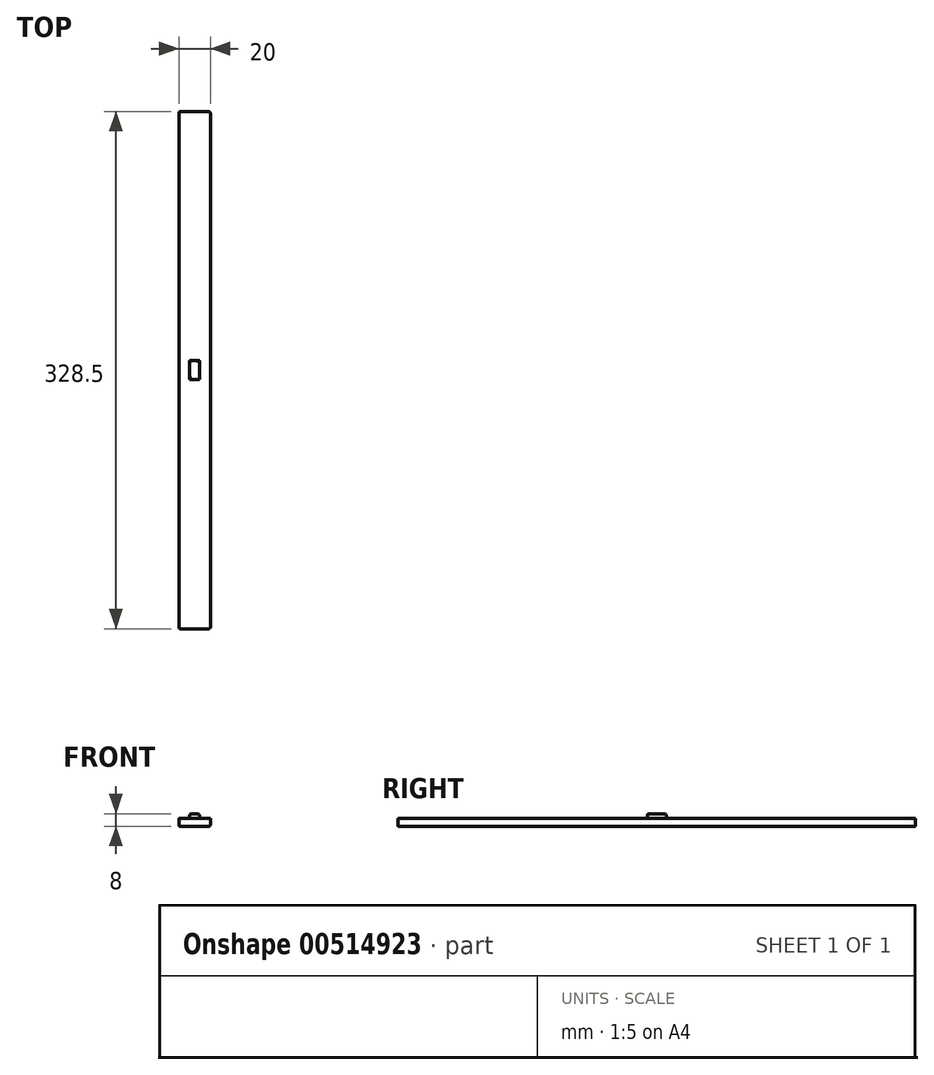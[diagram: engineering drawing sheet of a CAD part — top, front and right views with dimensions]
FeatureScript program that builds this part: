
annotation { "Feature Type Name" : "Feature", "Feature Type Description" : "" }
export const myFeature = defineFeature(function(context is Context, id is Id, definition is map)
    precondition{}
    {
        {
            var Q0;
            Q0=qCreatedBy(makeId("Top.planeOp"),FACE);
            var sketch = newSketch(context, id + "F0", { "sketchPlane" : qUnion([Q0])});
            skLineSegment(sketch, "E0.bottom", {"start": v(-10, 164.25) * mm, "end": v(10, 164.25) * mm});
            skLineSegment(sketch, "E0.top", {"start": v(-10, -164.25) * mm, "end": v(10, -164.25) * mm});
            skLineSegment(sketch, "E0.left", {"start": v(-10, 164.25) * mm, "end": v(-10, -164.25) * mm});
            skLineSegment(sketch, "E0.right", {"start": v(10, 164.25) * mm, "end": v(10, -164.25) * mm});
            skPoint(sketch, "E0.middle", {"position": v(0, 0) * mm});
            skLineSegment(sketch, "E1.bottom", {"start": v(3.05, 6) * mm, "end": v(-3.05, 6) * mm});
            skLineSegment(sketch, "E1.top", {"start": v(3.05, -6) * mm, "end": v(-3.05, -6) * mm});
            skLineSegment(sketch, "E1.left", {"start": v(3.05, 6) * mm, "end": v(3.05, -6) * mm});
            skLineSegment(sketch, "E1.right", {"start": v(-3.05, 6) * mm, "end": v(-3.05, -6) * mm});
            skSolve(sketch);
        }
        {
            var Q0;
            Q0 = qSketchRegion(id + "F0", true);
            extrude(context, id + "F1", {"entities" : qUnion([Q0]), "depth" : 5 * mm, "offsetDistance" : 25 * mm});
        }
        {
            var Q0;
            Q0=makeQuery(id+"F0.imprint","IMPRINT",FACE,{"disambiguationData":[TD([[makeQuery(id+"F0.imprint","IMPRINT",EDGE,{"derivedFrom":sQuery(id+"F0.wireOp",EDGE,"E1.bottom")}),1.0]])]});
            extrude(context, id + "F2", {"entities" : qUnion([Q0]), "operationType" : NewBodyOperationType.ADD, "depth" : 8 * mm, "offsetDistance" : 25 * mm});
        }
        {
            var Q0;
            Q0=makeQuery(id+"F2.opExtrude","CAP_EDGE",EDGE,{"disambiguationData":[OSD([sQuery(id+"F0.wireOp",EDGE,"E1.left")])],"isStart":false});
            var Q1;
            Q1=makeQuery(id+"F2.opExtrude","CAP_EDGE",EDGE,{"disambiguationData":[OSD([sQuery(id+"F0.wireOp",EDGE,"E1.right")])],"isStart":false});
            var Q2;
            Q2=makeQuery(id+"F2.opExtrude","CAP_EDGE",EDGE,{"disambiguationData":[OSD([sQuery(id+"F0.wireOp",EDGE,"E1.bottom")])],"isStart":false});
            var Q3;
            Q3=makeQuery(id+"F2.opExtrude","CAP_EDGE",EDGE,{"disambiguationData":[OSD([sQuery(id+"F0.wireOp",EDGE,"E1.top")])],"isStart":false});
            var Q4;
            Q4=makeQuery(id+"F1.opExtrude","CAP_EDGE",EDGE,{"disambiguationData":[OSD([sQuery(id+"F0.wireOp",EDGE,"E0.left")])],"isStart":true});
            var Q5;
            Q5=makeQuery(id+"F1.opExtrude","CAP_EDGE",EDGE,{"disambiguationData":[OSD([sQuery(id+"F0.wireOp",EDGE,"E0.right")])],"isStart":true});
            var Q6;
            Q6=makeQuery(id+"F1.opExtrude","SWEPT_EDGE",EDGE,{"disambiguationData":[OSD([sQuery(id+"F0.wireOp",EDGE,"E0.top"),sQuery(id+"F0.wireOp",EDGE,"E0.left")])]});
            var Q7;
            Q7=makeQuery(id+"F1.opExtrude","SWEPT_EDGE",EDGE,{"disambiguationData":[OSD([sQuery(id+"F0.wireOp",EDGE,"E0.top"),sQuery(id+"F0.wireOp",EDGE,"E0.right")])]});
            var Q8;
            Q8=makeQuery(id+"F1.opExtrude","SWEPT_EDGE",EDGE,{"disambiguationData":[OSD([sQuery(id+"F0.wireOp",EDGE,"E0.bottom"),sQuery(id+"F0.wireOp",EDGE,"E0.right")])]});
            var Q9;
            Q9=makeQuery(id+"F1.opExtrude","SWEPT_EDGE",EDGE,{"disambiguationData":[OSD([sQuery(id+"F0.wireOp",EDGE,"E0.bottom"),sQuery(id+"F0.wireOp",EDGE,"E0.left")])]});
            fillet(context, id + "F3", {"entities" : qUnion([Q0, Q1, Q2, Q3, Q4, Q5, Q6, Q7, Q8, Q9]), "radius" : 1 * mm, "allowEdgeOverflow" : false});
        }
    });
